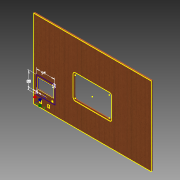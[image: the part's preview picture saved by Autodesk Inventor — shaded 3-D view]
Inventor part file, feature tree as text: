
AUTODESK INVENTOR PART (.ipt)
format: ipt  version: 2015 SP1 (Build 190203100, 203)  size: 751,616 bytes
history: native  units: in
note: dims shown in document units (in); Inventor stores cm internally (conversion verified against a paired STEP export)
features: reference x13, sketch x5, extrude x4, projected_geometry x2
ambient origin geometry x8: Origin, YZ Plane, XZ Plane, XY Plane, X Axis, Y Axis, Z Axis, Center Point
bodies: Solid1 (feature_tree)
feature tree (24):
  extrude  "Extrusion1"  Depth=0.1575in TaperAngle=0.0deg
  extrude  "Extrusion2"  Depth=0.7874in
  extrude  "Extrusion3"  Depth=0.4331in
  sketch  "Sketch5"  dims[d8=1.1811in d9=0.4331in]
  extrude  "Extrusion4"  Depth=0.4331in
  sketch  "Sketch2"  dims[d0=0.315in d1=0.0in d2=0.1575in d3=0.0in]
  reference  "Reference3"
  reference  "Reference4"
  reference  "Reference5"
  reference  "Reference6"
  reference  "Reference7"
  sketch  "Sketch3"  dims[d4=1.1811in d5=0.7874in]
  reference  "Reference8"
  reference  "Reference9"
  reference  "Reference10"
  reference  "Reference11"
  reference  "Reference12"
  reference  "Reference13"
  reference  "Reference14"
  reference  "Reference15"
  sketch  "Sketch4"  dims[d6=0.5315in d7=0.4331in]
  sketch  "Sketch6"  dims[d10=0.5906in d11=0.5906in d12=1.063in d13=2.0079in d14=0.315in d15=3.7008in d16=3.1102in d17=0.2756in d19=3.1791in d20=0.3543in d21=0.1575in d22=0.0in d23=3.4646in d24=3.7008in d25=0.315in d26=0.3937in d27=3.7008in d28=3.4646in d29=0.315in d30=0.3937in d31=0.1378in d32=0.0in]
  projected_geometry  "Project Cut Edges1"
  projected_geometry  "Project Cut Edges2"
